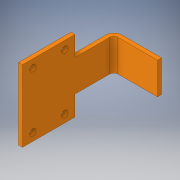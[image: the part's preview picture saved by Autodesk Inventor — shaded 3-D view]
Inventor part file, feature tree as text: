
AUTODESK INVENTOR PART (.ipt)
format: ipt  version: 2017 SP1 (Build 210196100, 196)  size: 132,608 bytes
history: native  units: in
note: dims shown in document units (in); Inventor stores cm internally (conversion verified against a paired STEP export)
features: extrude x2, sketch x2, fillet x1
ambient origin geometry x8: Origin, YZ Plane, XZ Plane, XY Plane, X Axis, Y Axis, Z Axis, Center Point
bodies: Solid1 (feature_tree)
feature tree (5):
  extrude  "Extrusion1"  Depth=3.0in
  extrude  "Extrusion2"  Depth=2.25in TaperAngle=0.0deg
  fillet  "Fillet1"  Radius=1.0in
  sketch  "Sketch1"  dims[d0=1.5in d1=3.0in]
  sketch  "Sketch2"  dims[d2=0.125in d3=2.25in d4=0.0in d5=1.0in d6=1.75in d8=0.2in d9=1.0in d10=1.65in d11=1.0in d12=0.0in d13=0.125in d14=0.25in]
